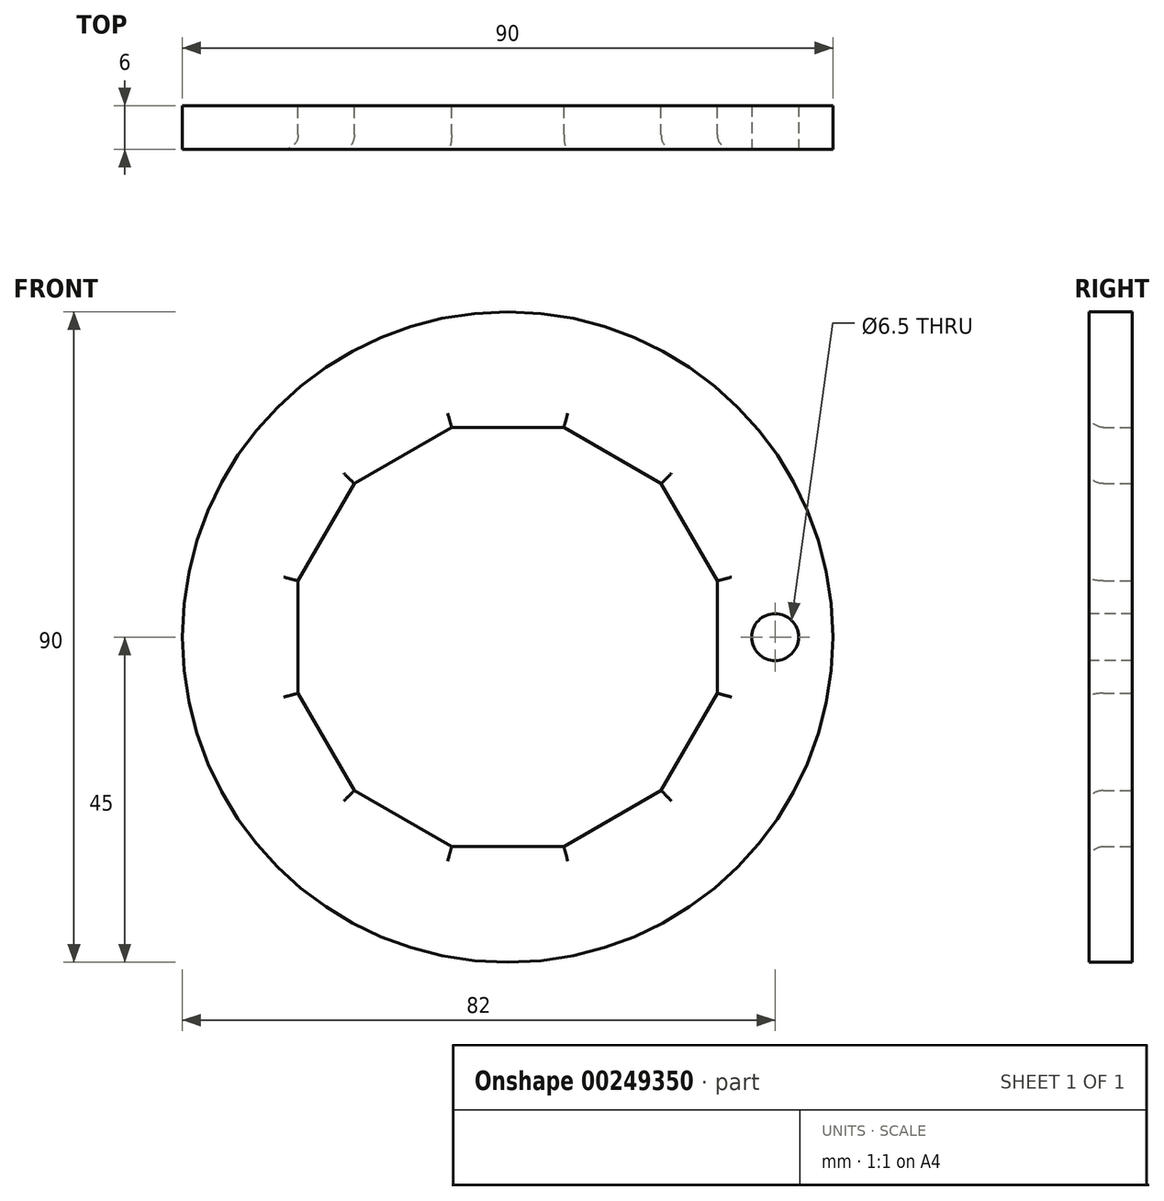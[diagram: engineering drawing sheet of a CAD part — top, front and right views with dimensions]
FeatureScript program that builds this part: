
annotation { "Feature Type Name" : "Feature", "Feature Type Description" : "" }
export const myFeature = defineFeature(function(context is Context, id is Id, definition is map)
    precondition{}
    {
        {
            var Q0;
            Q0=qCreatedBy(makeId("Front.planeOp"),FACE);
            var sketch = newSketch(context, id + "F0", { "sketchPlane" : qUnion([Q0])});
            skCircle(sketch, "E0.cCircle", {"center": v(0, 0) * mm, "radius": 29 * mm, "construction": true});
            skLineSegment(sketch, "E0.0", {"start": v(-7.77, 29) * mm, "end": v(7.77, 29) * mm});
            skLineSegment(sketch, "E0.1", {"start": v(7.77, 29) * mm, "end": v(21.23, 21.23) * mm});
            skLineSegment(sketch, "E0.2", {"start": v(21.23, 21.23) * mm, "end": v(29, 7.77) * mm});
            skLineSegment(sketch, "E0.3", {"start": v(29, 7.77) * mm, "end": v(29, -7.77) * mm});
            skLineSegment(sketch, "E0.4", {"start": v(29, -7.77) * mm, "end": v(21.23, -21.23) * mm});
            skLineSegment(sketch, "E0.5", {"start": v(21.23, -21.23) * mm, "end": v(7.77, -29) * mm});
            skLineSegment(sketch, "E0.6", {"start": v(7.77, -29) * mm, "end": v(-7.77, -29) * mm});
            skLineSegment(sketch, "E0.7", {"start": v(-7.77, -29) * mm, "end": v(-21.23, -21.23) * mm});
            skLineSegment(sketch, "E0.8", {"start": v(-21.23, -21.23) * mm, "end": v(-29, -7.77) * mm});
            skLineSegment(sketch, "E0.9", {"start": v(-29, -7.77) * mm, "end": v(-29, 7.77) * mm});
            skLineSegment(sketch, "E0.10", {"start": v(-29, 7.77) * mm, "end": v(-21.23, 21.23) * mm});
            skLineSegment(sketch, "E0.11", {"start": v(-21.23, 21.23) * mm, "end": v(-7.77, 29) * mm});
            skPoint(sketch, "E0.0.midPoint", {"position": v(0, 29) * mm});
            skCircle(sketch, "E1", {"center": v(0, 0) * mm, "radius": 45 * mm});
            skSolve(sketch);
        }
        {
            var Q0;
            Q0=makeQuery(id+"F0.imprint","IMPRINT",FACE,{"disambiguationData":[TD([[makeQuery(id+"F0.imprint","IMPRINT",EDGE,{"derivedFrom":sQuery(id+"F0.wireOp",EDGE,"E0.0")}),1.0]])]});
            extrude(context, id + "F1", {"entities" : qUnion([Q0]), "depth" : 6 * mm, "symmetric" : true});
        }
        {
            var Q0;
            Q0=makeQuery(id+"F1.opExtrude","CAP_EDGE",EDGE,{"disambiguationData":[OSD([sQuery(id+"F0.wireOp",EDGE,"E0.11")])],"isStart":false});
            var Q1;
            Q1=makeQuery(id+"F1.opExtrude","CAP_EDGE",EDGE,{"disambiguationData":[OSD([sQuery(id+"F0.wireOp",EDGE,"E0.0")])],"isStart":false});
            var Q2;
            Q2=makeQuery(id+"F1.opExtrude","CAP_EDGE",EDGE,{"disambiguationData":[OSD([sQuery(id+"F0.wireOp",EDGE,"E0.1")])],"isStart":false});
            var Q3;
            Q3=makeQuery(id+"F1.opExtrude","CAP_EDGE",EDGE,{"disambiguationData":[OSD([sQuery(id+"F0.wireOp",EDGE,"E0.2")])],"isStart":false});
            var Q4;
            Q4=makeQuery(id+"F1.opExtrude","CAP_EDGE",EDGE,{"disambiguationData":[OSD([sQuery(id+"F0.wireOp",EDGE,"E0.3")])],"isStart":false});
            var Q5;
            Q5=makeQuery(id+"F1.opExtrude","CAP_EDGE",EDGE,{"disambiguationData":[OSD([sQuery(id+"F0.wireOp",EDGE,"E0.4")])],"isStart":false});
            var Q6;
            Q6=makeQuery(id+"F1.opExtrude","CAP_EDGE",EDGE,{"disambiguationData":[OSD([sQuery(id+"F0.wireOp",EDGE,"E0.5")])],"isStart":false});
            var Q7;
            Q7=makeQuery(id+"F1.opExtrude","CAP_EDGE",EDGE,{"disambiguationData":[OSD([sQuery(id+"F0.wireOp",EDGE,"E0.6")])],"isStart":false});
            var Q8;
            Q8=makeQuery(id+"F1.opExtrude","CAP_EDGE",EDGE,{"disambiguationData":[OSD([sQuery(id+"F0.wireOp",EDGE,"E0.7")])],"isStart":false});
            var Q9;
            Q9=makeQuery(id+"F1.opExtrude","CAP_EDGE",EDGE,{"disambiguationData":[OSD([sQuery(id+"F0.wireOp",EDGE,"E0.8")])],"isStart":false});
            var Q10;
            Q10=makeQuery(id+"F1.opExtrude","CAP_EDGE",EDGE,{"disambiguationData":[OSD([sQuery(id+"F0.wireOp",EDGE,"E0.9")])],"isStart":false});
            var Q11;
            Q11=makeQuery(id+"F1.opExtrude","CAP_EDGE",EDGE,{"disambiguationData":[OSD([sQuery(id+"F0.wireOp",EDGE,"E0.10")])],"isStart":false});
            fillet(context, id + "F2", {"entities" : qUnion([Q0, Q1, Q2, Q3, Q4, Q5, Q6, Q7, Q8, Q9, Q10, Q11]), "radius" : 2 * mm, "tangentPropagation" : true, "allowEdgeOverflow" : false});
        }
        {
            var Q0;
            Q0=qCreatedBy(makeId("Front.planeOp"),FACE);
            var sketch = newSketch(context, id + "F3", { "sketchPlane" : qUnion([Q0])});
            skCircle(sketch, "E2", {"center": v(37, 0) * mm, "radius": 3.25 * mm});
            skSolve(sketch);
        }
        {
            var Q0;
            Q0 = qSketchRegion(id + "F3", true);
            extrude(context, id + "F4", {"entities" : qUnion([Q0]), "operationType" : NewBodyOperationType.REMOVE, "oppositeDirection" : true, "depth" : 25 * mm, "symmetric" : true});
        }
    });
